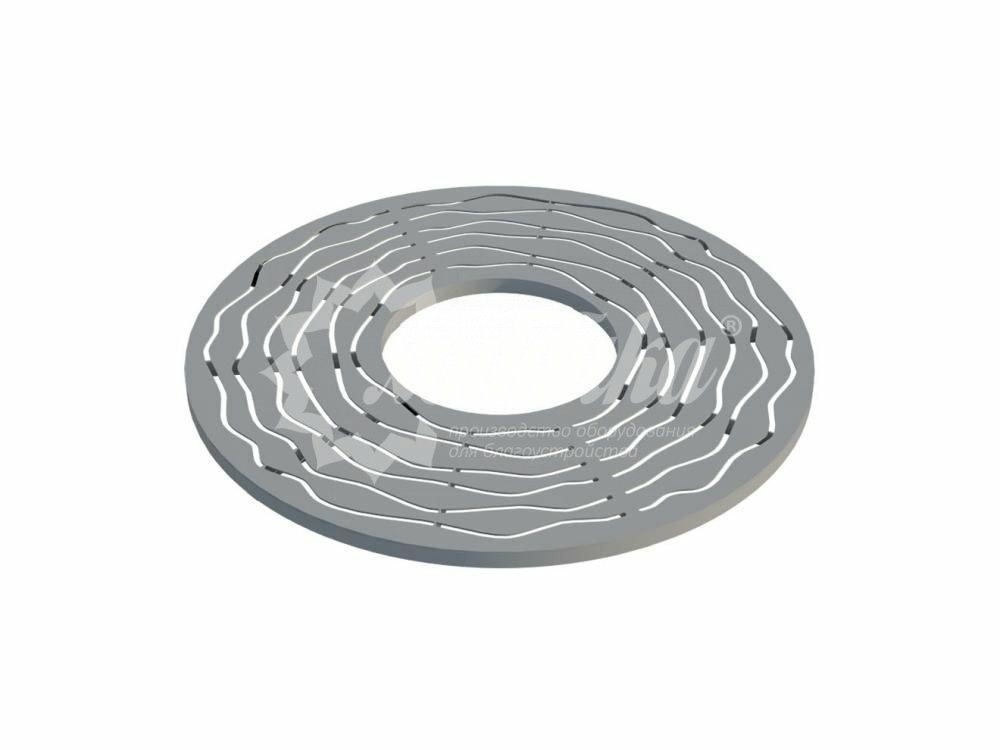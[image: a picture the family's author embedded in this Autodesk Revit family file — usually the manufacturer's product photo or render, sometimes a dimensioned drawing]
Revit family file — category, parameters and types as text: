
# Revit family: Приствольная решетка «Танго» Арт 15528
name_source: partatom
category: Антураж
revit_build: Autodesk Revit 2018 (Build: 20180423_1000(x64)
units: mm (PartAtom-declared; Revit-internal decimal feet)

## family parameters
Всегда вертикально = Да
Источник визуального образа = Геометрия семейства
На основе рабочей плоскости = Нет
Общий = Нет
При загрузке вырезать с полостями = Нет
Точка расчета площади = Нет

## types (2) — shared parameters
URL = https://hobbyka.ru
Артикул товара = Арт. 15528
Высота = 50 мм
Группа модели = Решётки для деревьев
Изготовитель = ООО «Хоббика»
Изображение типоразмера = решетка для дерева ТАНГО.jpg
Материал изделия = Сталь
Цвет покраски = <По категории>

## per-type parameters (varying)
| type | Диаметр внеш. | Диаметр внут. | Модель 1,0 м | Модель 1,5 м | Описание |
| Приствольная решетка «Танго» Модель 1,0 м | 1000 мм | 500 мм | Да | Нет | Приствольная решетка «Танго», модель, 1,0 м |
| Приствольная решетка «Танго» Модель 1,5 м | 1500 мм | 700 мм | Нет | Да | Приствольная решетка «Танго», модель, 1,5 м |
